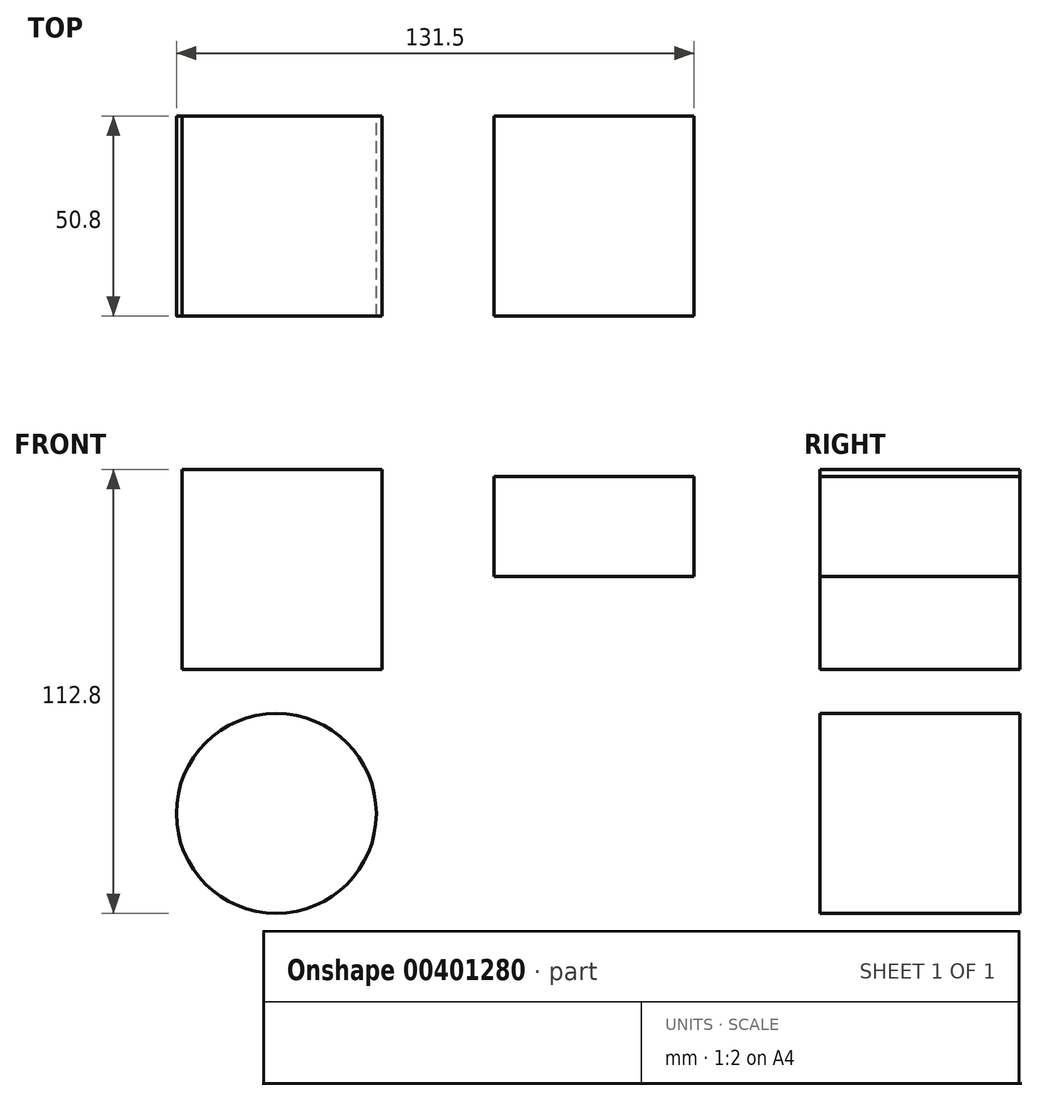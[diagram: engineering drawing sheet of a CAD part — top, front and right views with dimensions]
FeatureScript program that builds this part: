
annotation { "Feature Type Name" : "Feature", "Feature Type Description" : "" }
export const myFeature = defineFeature(function(context is Context, id is Id, definition is map)
    precondition{}
    {
        {
            var Q0;
            Q0=qCreatedBy(makeId("Front.planeOp"),FACE);
            var sketch = newSketch(context, id + "F0", { "sketchPlane" : qUnion([Q0])});
            skLineSegment(sketch, "E0.bottom", {"start": v(-70.29, 59.26) * mm, "end": v(-19.49, 59.26) * mm});
            skLineSegment(sketch, "E0.top", {"start": v(-70.29, 8.46) * mm, "end": v(-19.49, 8.46) * mm});
            skLineSegment(sketch, "E0.left", {"start": v(-70.29, 59.26) * mm, "end": v(-70.29, 8.46) * mm});
            skLineSegment(sketch, "E0.right", {"start": v(-19.49, 59.26) * mm, "end": v(-19.49, 8.46) * mm});
            skSolve(sketch);
        }
        {
            var Q0;
            Q0=qCreatedBy(makeId("Front.planeOp"),FACE);
            var sketch = newSketch(context, id + "F1", { "sketchPlane" : qUnion([Q0])});
            skLineSegment(sketch, "E1.bottom", {"start": v(9.02, 57.47) * mm, "end": v(59.82, 57.47) * mm});
            skLineSegment(sketch, "E1.top", {"start": v(9.02, 32.07) * mm, "end": v(59.82, 32.07) * mm});
            skLineSegment(sketch, "E1.left", {"start": v(9.02, 57.47) * mm, "end": v(9.02, 32.07) * mm});
            skLineSegment(sketch, "E1.right", {"start": v(59.82, 57.47) * mm, "end": v(59.82, 32.07) * mm});
            skSolve(sketch);
        }
        {
            var Q0;
            Q0=qCreatedBy(makeId("Front.planeOp"),FACE);
            var sketch = newSketch(context, id + "F2", { "sketchPlane" : qUnion([Q0])});
            skCircle(sketch, "E2", {"center": v(-46.28, -28.14) * mm, "radius": 25.4 * mm});
            skSolve(sketch);
        }
        {
            var Q0;
            Q0=makeQuery(id+"F0.imprint","IMPRINT",FACE,{"disambiguationData":[TD([[makeQuery(id+"F0.imprint","IMPRINT",EDGE,{"derivedFrom":sQuery(id+"F0.wireOp",EDGE,"E0.bottom")}),-1.0]])]});
            extrude(context, id + "F3", {"entities" : qUnion([Q0]), "depth" : 50.8 * mm});
        }
        {
            var Q0;
            Q0=makeQuery(id+"F1.imprint","IMPRINT",FACE,{"disambiguationData":[TD([[makeQuery(id+"F1.imprint","IMPRINT",EDGE,{"derivedFrom":sQuery(id+"F1.wireOp",EDGE,"E1.bottom")}),-1.0]])]});
            extrude(context, id + "F4", {"entities" : qUnion([Q0]), "depth" : 50.8 * mm});
        }
        {
            var Q0;
            Q0=makeQuery(id+"F2.imprint","IMPRINT",FACE,{"disambiguationData":[TD([[makeQuery(id+"F2.imprint","IMPRINT",EDGE,{"derivedFrom":sQuery(id+"F2.wireOp",EDGE,"E2")}),1.0]])]});
            extrude(context, id + "F5", {"entities" : qUnion([Q0]), "depth" : 50.8 * mm});
        }
    });
